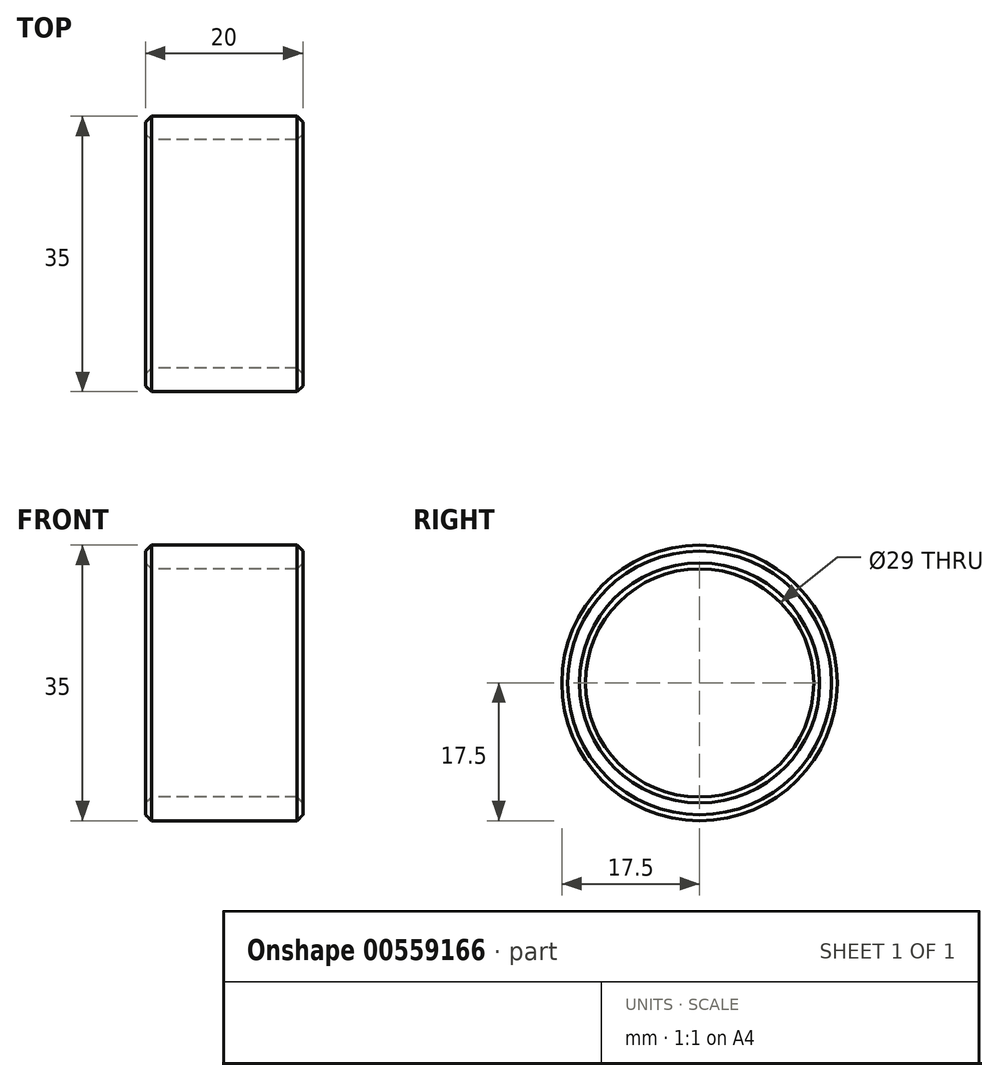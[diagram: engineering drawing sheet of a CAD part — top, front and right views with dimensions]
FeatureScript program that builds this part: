
annotation { "Feature Type Name" : "Feature", "Feature Type Description" : "" }
export const myFeature = defineFeature(function(context is Context, id is Id, definition is map)
    precondition{}
    {
        {
            var Q0;
            Q0=qCreatedBy(makeId("Right.planeOp"),FACE);
            var sketch = newSketch(context, id + "F0", { "sketchPlane" : qUnion([Q0])});
            skCircle(sketch, "E0", {"center": v(0, 0) * mm, "radius": 17.5 * mm});
            skCircle(sketch, "E1", {"center": v(0, 0) * mm, "radius": 14.5 * mm});
            skSolve(sketch);
        }
        {
            var Q0;
            Q0 = qSketchRegion(id + "F0", true);
            extrude(context, id + "F1", {"entities" : qUnion([Q0]), "endBound" : BoundingType.SYMMETRIC, "depth" : 20 * mm, "offsetDistance" : 25 * mm});
        }
        {
            var Q0;
            Q0=makeQuery(id+"F1.opExtrude","CAP_EDGE",EDGE,{"disambiguationData":[OSD([sQuery(id+"F0.wireOp",EDGE,"E0")])],"isStart":true});
            var Q1;
            Q1=makeQuery(id+"F1.opExtrude","CAP_EDGE",EDGE,{"disambiguationData":[OSD([sQuery(id+"F0.wireOp",EDGE,"E0")])],"isStart":false});
            var Q2;
            Q2=makeQuery(id+"F1.opExtrude","CAP_EDGE",EDGE,{"disambiguationData":[OSD([sQuery(id+"F0.wireOp",EDGE,"E1")])],"isStart":false});
            var Q3;
            Q3=makeQuery(id+"F1.opExtrude","CAP_EDGE",EDGE,{"disambiguationData":[OSD([sQuery(id+"F0.wireOp",EDGE,"E1")])],"isStart":true});
            chamfer(context, id + "F2", {"entities" : qUnion([Q0, Q1, Q2, Q3]), "width" : 0.75 * mm, "tangentPropagation" : true});
        }
    });
